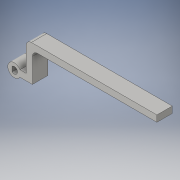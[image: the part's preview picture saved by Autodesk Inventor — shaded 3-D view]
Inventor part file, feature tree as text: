
AUTODESK INVENTOR PART (.ipt)
format: ipt  version: 2016 SP1 (Build 200210100, 210)  size: 141,312 bytes
history: native  units: in
note: dims shown in document units (in); Inventor stores cm internally (conversion verified against a paired STEP export)
features: extrude x5, sketch x5, fillet x2
ambient origin geometry x8: Origin, YZ Plane, XZ Plane, XY Plane, X Axis, Y Axis, Z Axis, Center Point
bodies: Body1 (feature_tree)
feature tree (12):
  extrude  "Extrusion2"  Depth=0.1575in
  extrude  "Extrusion3"  Depth=0.158in
  extrude  "Extrusion4"  Depth=0.37in TaperAngle=0.0deg
  extrude  "Extrusion5"  Depth=0.15in
  fillet  "Fillet1"  Radius=0.37in
  fillet  "Fillet2"  Radius=0.7059in
  extrude  "Extrusion6"  Depth=0.125in
  sketch  "Sketch2"  dims[d7=0.1575in d8=0.315in]
  sketch  "Sketch3"  dims[d9=0.1in d10=0.158in]
  sketch  "Sketch4"  dims[d11=0.0787in d12=0.37in d13=0.0in]
  sketch  "Sketch5"  dims[d14=0.2in d15=0.0in d16=0.15in d17=0.37in d18=0.7059in d19=0.0in]
  sketch  "Sketch6"  dims[d21=3.0in d22=0.0in d23=0.125in d24=0.125in d25=0.052in d26=0.052in d27=0.37in d28=0.0in d29=0.37in d30=0.1537in d31=0.1537in]
